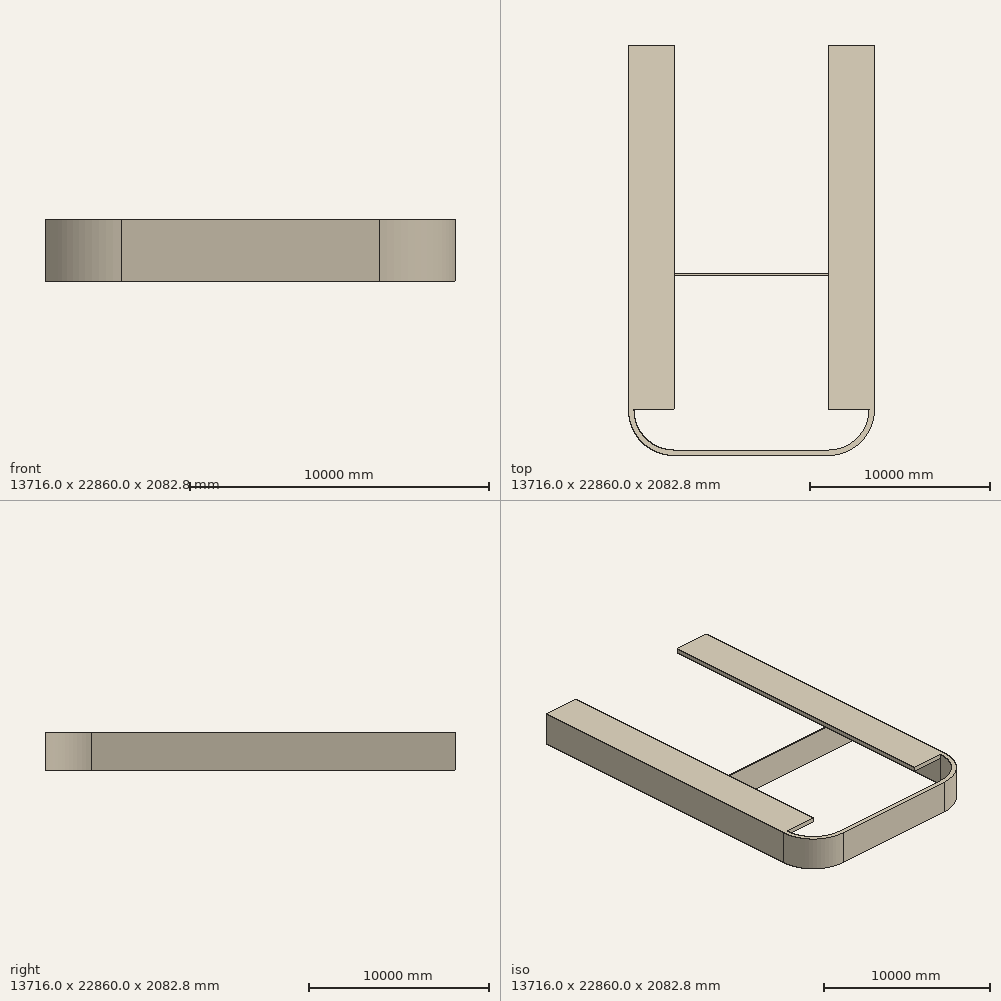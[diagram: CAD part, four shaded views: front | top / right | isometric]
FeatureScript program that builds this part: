
annotation { "Feature Type Name" : "Feature", "Feature Type Description" : "" }
export const myFeature = defineFeature(function(context is Context, id is Id, definition is map)
    precondition{}
    {
        {
            var Q0;
            Q0=qCreatedBy(makeId("Front.planeOp"),FACE);
            var sketch = newSketch(context, id + "F0", { "sketchPlane" : qUnion([Q0])});
            skLineSegment(sketch, "E0", {"start": v(4318, 2082.8) * mm, "end": v(4318, 1828.8) * mm});
            skLineSegment(sketch, "E1", {"start": v(4318, 1828.8) * mm, "end": v(6553.2, 1828.8) * mm});
            skLineSegment(sketch, "E2", {"start": v(6553.2, 1828.8) * mm, "end": v(6553.2, 0) * mm});
            skLineSegment(sketch, "E3", {"start": v(6553.2, 0) * mm, "end": v(6858, 0) * mm});
            skLineSegment(sketch, "E4", {"start": v(6858, 0) * mm, "end": v(6858, 2082.8) * mm});
            skLineSegment(sketch, "E5", {"start": v(6858, 2082.8) * mm, "end": v(4318, 2082.8) * mm});
            skSolve(sketch);
        }
        {
            var Q0;
            Q0 = qSketchRegion(id + "F0", true);
            extrude(context, id + "F1", {"entities" : qUnion([Q0]), "oppositeDirection" : true, "depth" : 20320 * mm});
        }
        {
            var Q0;
            Q0=makeQuery(id+"F1.opExtrude","SWEPT_BODY",BODY,{"disambiguationData":[OSD([sQuery(id+"F0.wireOp",EDGE,"E0"),sQuery(id+"F0.wireOp",EDGE,"E1"),sQuery(id+"F0.wireOp",EDGE,"E2"),sQuery(id+"F0.wireOp",EDGE,"E3"),sQuery(id+"F0.wireOp",EDGE,"E4"),sQuery(id+"F0.wireOp",EDGE,"E5")])]});
            var Q1;
            Q1=qCreatedBy(makeId("Right.planeOp"),FACE);
            mirror(context, id + "F2", {"entities" : qUnion([Q0]), "mirrorPlane" : qUnion([Q1])});
        }
        {
            var Q0;
            Q0=makeQuery(id+"F2.opPattern","COPY",FACE,{"derivedFrom":makeQuery(id+"F1.opExtrude","SWEPT_FACE",FACE,{"disambiguationData":[OSD([sQuery(id+"F0.wireOp",EDGE,"E2")])]}),"instanceName":"1"});
            var sketch = newSketch(context, id + "F3", { "sketchPlane" : qUnion([Q0])});
            skLineSegment(sketch, "E6", {"start": v(7493, 1828.8) * mm, "end": v(7493, 0) * mm});
            skLineSegment(sketch, "E7", {"start": v(7493, 0) * mm, "end": v(7620, 0) * mm});
            skLineSegment(sketch, "E8", {"start": v(7620, 0) * mm, "end": v(7620, 1828.8) * mm});
            skLineSegment(sketch, "E9", {"start": v(7620, 1828.8) * mm, "end": v(7493, 1828.8) * mm});
            skSolve(sketch);
        }
        {
            var Q0;
            Q0 = qSketchRegion(id + "F3", true);
            extrude(context, id + "F4", {"entities" : qUnion([Q0]), "operationType" : NewBodyOperationType.ADD, "depth" : 13106.4 * mm});
        }
        {
            var Q0;
            Q0=makeQuery(id+"F2.opPattern","COPY",FACE,{"derivedFrom":makeQuery(id+"F1.opExtrude","SWEPT_FACE",FACE,{"disambiguationData":[OSD([sQuery(id+"F0.wireOp",EDGE,"E5")])]}),"instanceName":"1"});
            var sketch = newSketch(context, id + "F5", { "sketchPlane" : qUnion([Q0])});
            skLineSegment(sketch, "E10", {"start": v(-6858, 0) * mm, "end": v(-6858, 0) * mm});
            skLineSegment(sketch, "E11.0", {"start": v(6858, 20320) * mm, "end": v(6858, 0) * mm, "construction": true});
            skLineSegment(sketch, "E12", {"start": v(6858, 0) * mm, "end": v(6858, 0) * mm});
            skLineSegment(sketch, "E13", {"start": v(-4318, -2540) * mm, "end": v(4318, -2540) * mm});
            skPoint(sketch, "E14.visualSharp", {"position": v(-6858, -2540) * mm});
            skArc(sketch, "E14.filletArc", {"start": v(-6858, -2533.65) * mm, "mid": v(-6856.14, -2538.14) * mm, "end": v(-6851.65, -2540) * mm});
            skArc(sketch, "E15.filletArc", {"start": v(-6858, 0) * mm, "mid": v(-6114.05, -1796.05) * mm, "end": v(-4318, -2540) * mm});
            skPoint(sketch, "E16.visualSharp", {"position": v(6858, -2540) * mm});
            skArc(sketch, "E16.filletArc", {"start": v(4318, -2540) * mm, "mid": v(6114.05, -1796.05) * mm, "end": v(6858, 0) * mm});
            skSolve(sketch);
        }
        {
            var Q0;
            Q0=makeQuery(id+"F2.opPattern","COPY",FACE,{"derivedFrom":makeQuery(id+"F1.opExtrude","CAP_FACE",FACE,{"disambiguationData":[OSD([sQuery(id+"F0.wireOp",EDGE,"E0"),sQuery(id+"F0.wireOp",EDGE,"E1"),sQuery(id+"F0.wireOp",EDGE,"E2"),sQuery(id+"F0.wireOp",EDGE,"E3"),sQuery(id+"F0.wireOp",EDGE,"E4"),sQuery(id+"F0.wireOp",EDGE,"E5")])],"isStart":true}),"instanceName":"1"});
            var sketch = newSketch(context, id + "F6", { "sketchPlane" : qUnion([Q0])});
            skLineSegment(sketch, "E17.bottom", {"start": v(-6858, 0) * mm, "end": v(-6553.2, 0) * mm});
            skLineSegment(sketch, "E17.top", {"start": v(-6858, 2082.8) * mm, "end": v(-6553.2, 2082.8) * mm});
            skLineSegment(sketch, "E17.left", {"start": v(-6858, 0) * mm, "end": v(-6858, 2082.8) * mm});
            skLineSegment(sketch, "E17.right", {"start": v(-6553.2, 0) * mm, "end": v(-6553.2, 2082.8) * mm});
            skSolve(sketch);
        }
        {
            var Q0;
            {var subQ2=sQuery(id+"F6.wireOp",EDGE,"E17.bottom");Q0=makeQuery(id+"F6.imprint","IMPRINT",FACE,{"disambiguationData":[TD([[makeQuery(id+"F6.imprint","IMPRINT",EDGE,{"derivedFrom":subQ2}),-1.0]])]});}
            var Q1;
            Q1=sQuery(id+"F5.wireOp",EDGE,"E15.filletArc");
            var Q2;
            Q2=sQuery(id+"F5.wireOp",EDGE,"E13");
            var Q3;
            Q3=sQuery(id+"F5.wireOp",EDGE,"E16.filletArc");
            sweep(context, id + "F7", {"operationType" : NewBodyOperationType.ADD, "profiles" : qUnion([Q0]), "path" : qUnion([Q1, Q2, Q3])});
        }
    });
